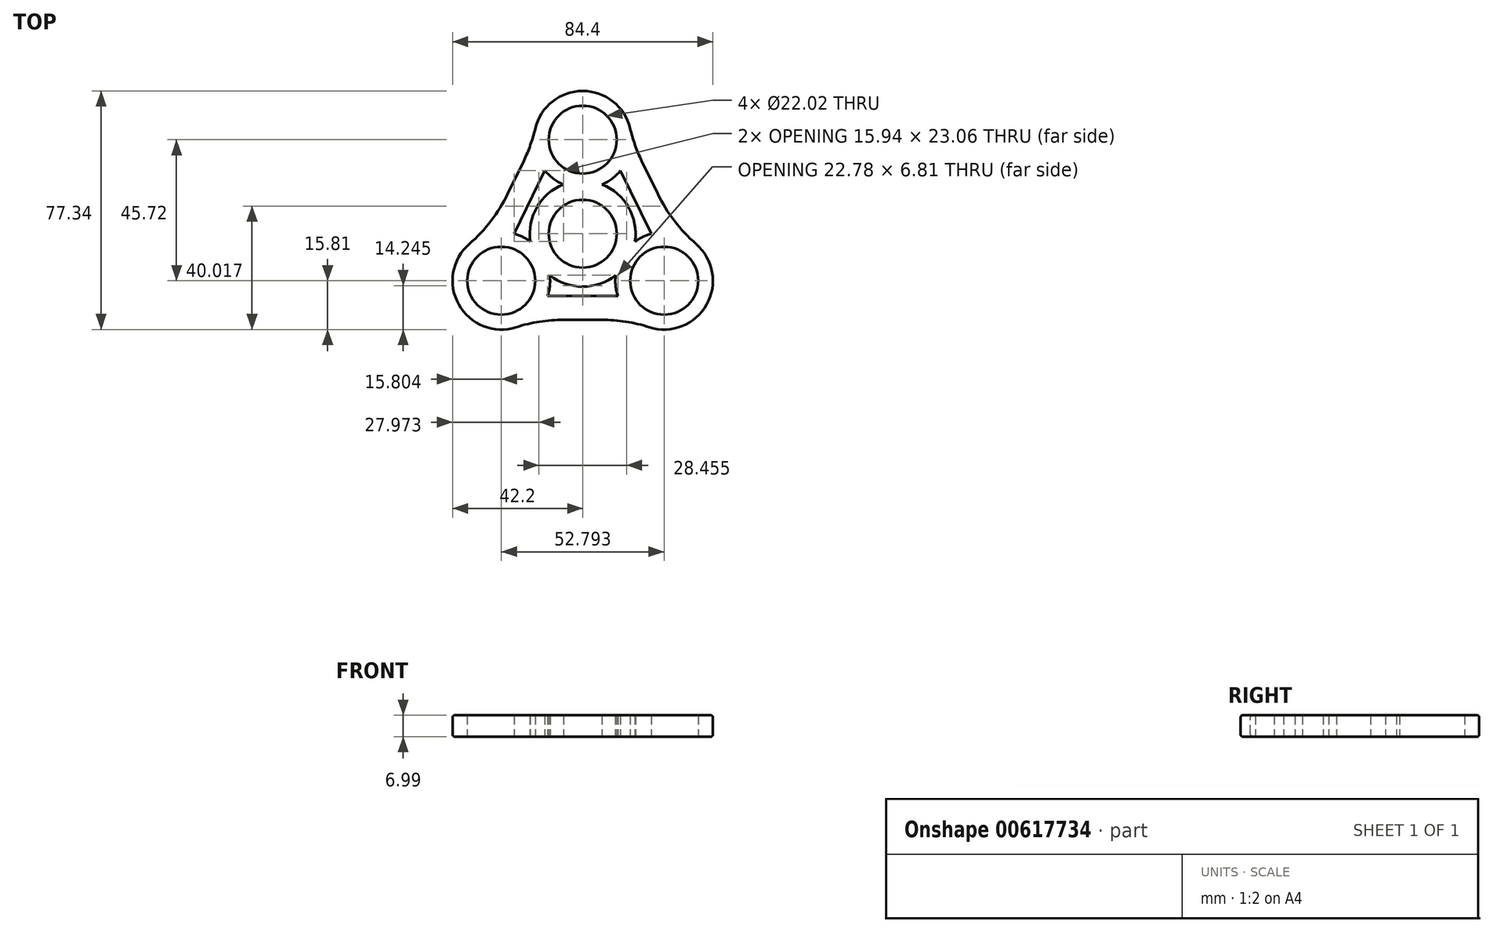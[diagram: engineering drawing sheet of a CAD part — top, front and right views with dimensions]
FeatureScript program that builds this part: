
annotation { "Feature Type Name" : "Feature", "Feature Type Description" : "" }
export const myFeature = defineFeature(function(context is Context, id is Id, definition is map)
    precondition{}
    {
        {
            var Q0;
            Q0=qCreatedBy(makeId("Top.planeOp"),FACE);
            var sketch = newSketch(context, id + "F0", { "sketchPlane" : qUnion([Q0])});
            skCircle(sketch, "E0", {"center": v(0, 0) * mm, "radius": 11.01 * mm});
            skLineSegment(sketch, "E1", {"start": v(0, 0) * mm, "end": v(0, 30.48) * mm});
            skLineSegment(sketch, "E2", {"start": v(0, 0) * mm, "end": v(26.4, -15.24) * mm});
            skLineSegment(sketch, "E3", {"start": v(0, 0) * mm, "end": v(-26.4, -15.24) * mm});
            skCircle(sketch, "E4", {"center": v(0, 30.48) * mm, "radius": 11.01 * mm});
            skCircle(sketch, "E5", {"center": v(26.4, -15.24) * mm, "radius": 11.01 * mm});
            skCircle(sketch, "E6", {"center": v(-26.4, -15.24) * mm, "radius": 11.01 * mm});
            skCircle(sketch, "E7", {"center": v(0, 30.48) * mm, "radius": 15.8 * mm});
            skCircle(sketch, "E8", {"center": v(26.4, -15.24) * mm, "radius": 15.8 * mm});
            skCircle(sketch, "E9", {"center": v(-26.4, -15.24) * mm, "radius": 15.8 * mm});
            skCircle(sketch, "E10", {"center": v(0, 0) * mm, "radius": 17.15 * mm});
            skLineSegment(sketch, "E11", {"start": v(15.8, 30.48) * mm, "end": v(30.6, 0) * mm});
            skLineSegment(sketch, "E12", {"start": v(-15.8, 30.48) * mm, "end": v(-30.6, 0) * mm});
            skLineSegment(sketch, "E13", {"start": v(-16.94, -27.9) * mm, "end": v(16.94, -27.9) * mm});
            skLineSegment(sketch, "E14", {"start": v(-12.26, 20.5) * mm, "end": v(-22.2, 0) * mm});
            skLineSegment(sketch, "E15", {"start": v(12.26, 20.5) * mm, "end": v(22.2, 0) * mm});
            skLineSegment(sketch, "E16", {"start": v(-11.4, -20.21) * mm, "end": v(11.4, -20.21) * mm});
            skSolve(sketch);
        }
        {
            var Q0;
            Q0 = qSketchRegion(id + "F0", true);
            var Q1;
            {var subQ1=sQuery(id+"F0.wireOp",EDGE,"E1");var subQ5=sQuery(id+"F0.wireOp",EDGE,"E0");var subQ6=makeQuery(id+"F0.imprint","INTERSECT",VERTEX,{"derivedFrom":[subQ5,subQ1]});Q1=makeQuery(id+"F0.imprint","IMPRINT",FACE,{"disambiguationData":[TD([[makeQuery(id+"F0.imprint","IMPRINT",EDGE,{"disambiguationData":[TD([[subQ6,1.0]])],"derivedFrom":subQ5}),-1.0]])]});}
            var Q2;
            {var subQ5=sQuery(id+"F0.wireOp",EDGE,"E3");var subQ6=sQuery(id+"F0.wireOp",EDGE,"E0");var subQ7=makeQuery(id+"F0.imprint","INTERSECT",VERTEX,{"derivedFrom":[subQ6,subQ5]});Q2=makeQuery(id+"F0.imprint","IMPRINT",FACE,{"disambiguationData":[TD([[makeQuery(id+"F0.imprint","IMPRINT",EDGE,{"disambiguationData":[TD([[subQ7,-1.0]])],"derivedFrom":subQ6}),-1.0]])]});}
            var Q3;
            {var subQ5=sQuery(id+"F0.wireOp",EDGE,"E0");var subQ7=sQuery(id+"F0.wireOp",EDGE,"E3");var subQ8=makeQuery(id+"F0.imprint","INTERSECT",VERTEX,{"derivedFrom":[subQ5,subQ7]});Q3=makeQuery(id+"F0.imprint","IMPRINT",FACE,{"disambiguationData":[TD([[makeQuery(id+"F0.imprint","IMPRINT",EDGE,{"disambiguationData":[TD([[subQ8,1.0]])],"derivedFrom":subQ5}),-1.0]])]});}
            var Q4;
            {var subQ0=sQuery(id+"F0.wireOp",EDGE,"E10");var subQ1=sQuery(id+"F0.wireOp",EDGE,"E2");var subQ2=makeQuery(id+"F0.imprint","INTERSECT",VERTEX,{"derivedFrom":[subQ1,subQ0]});Q4=makeQuery(id+"F0.imprint","IMPRINT",FACE,{"disambiguationData":[TD([[makeQuery(id+"F0.imprint","IMPRINT",EDGE,{"disambiguationData":[TD([[subQ2,1.0]])],"derivedFrom":subQ1}),-1.0]])]});}
            var Q5;
            {var subQ0=sQuery(id+"F0.wireOp",EDGE,"E10");var subQ1=sQuery(id+"F0.wireOp",EDGE,"E2");var subQ2=makeQuery(id+"F0.imprint","INTERSECT",VERTEX,{"derivedFrom":[subQ1,subQ0]});Q5=makeQuery(id+"F0.imprint","IMPRINT",FACE,{"disambiguationData":[TD([[makeQuery(id+"F0.imprint","IMPRINT",EDGE,{"disambiguationData":[TD([[subQ2,1.0]])],"derivedFrom":subQ1}),1.0]])]});}
            var Q6;
            {var subQ0=sQuery(id+"F0.wireOp",EDGE,"E10");var subQ1=sQuery(id+"F0.wireOp",EDGE,"E1");var subQ2=makeQuery(id+"F0.imprint","INTERSECT",VERTEX,{"derivedFrom":[subQ1,subQ0]});Q6=makeQuery(id+"F0.imprint","IMPRINT",FACE,{"disambiguationData":[TD([[makeQuery(id+"F0.imprint","IMPRINT",EDGE,{"disambiguationData":[TD([[subQ2,1.0]])],"derivedFrom":subQ1}),-1.0]])]});}
            var Q7;
            {var subQ0=sQuery(id+"F0.wireOp",EDGE,"E10");var subQ1=sQuery(id+"F0.wireOp",EDGE,"E1");var subQ2=makeQuery(id+"F0.imprint","INTERSECT",VERTEX,{"derivedFrom":[subQ1,subQ0]});Q7=makeQuery(id+"F0.imprint","IMPRINT",FACE,{"disambiguationData":[TD([[makeQuery(id+"F0.imprint","IMPRINT",EDGE,{"disambiguationData":[TD([[subQ2,1.0]])],"derivedFrom":subQ1}),1.0]])]});}
            var Q8;
            {var subQ0=sQuery(id+"F0.wireOp",EDGE,"E10");var subQ1=sQuery(id+"F0.wireOp",EDGE,"E3");var subQ2=makeQuery(id+"F0.imprint","INTERSECT",VERTEX,{"derivedFrom":[subQ1,subQ0]});Q8=makeQuery(id+"F0.imprint","IMPRINT",FACE,{"disambiguationData":[TD([[makeQuery(id+"F0.imprint","IMPRINT",EDGE,{"disambiguationData":[TD([[subQ2,1.0]])],"derivedFrom":subQ1}),-1.0]])]});}
            var Q9;
            {var subQ0=sQuery(id+"F0.wireOp",EDGE,"E10");var subQ1=sQuery(id+"F0.wireOp",EDGE,"E3");var subQ2=makeQuery(id+"F0.imprint","INTERSECT",VERTEX,{"derivedFrom":[subQ1,subQ0]});Q9=makeQuery(id+"F0.imprint","IMPRINT",FACE,{"disambiguationData":[TD([[makeQuery(id+"F0.imprint","IMPRINT",EDGE,{"disambiguationData":[TD([[subQ2,1.0]])],"derivedFrom":subQ1}),1.0]])]});}
            extrude(context, id + "F1", {"entities" : qUnion([Q0, Q1, Q2, Q3, Q4, Q5, Q6, Q7, Q8, Q9]), "depth" : 7 * mm, "offsetDistance" : 25.4 * mm});
        }
        {
            var Q0;
            Q0=makeQuery(id+"F1.opExtrude","SWEPT_EDGE",EDGE,{"disambiguationData":[OSD([sQuery(id+"F0.wireOp",EDGE,"E8"),sQuery(id+"F0.wireOp",EDGE,"E13")])]});
            var Q1;
            Q1=makeQuery(id+"F1.opExtrude","SWEPT_EDGE",EDGE,{"disambiguationData":[OSD([sQuery(id+"F0.wireOp",EDGE,"E9"),sQuery(id+"F0.wireOp",EDGE,"E13")])]});
            var Q2;
            Q2=makeQuery(id+"F1.opExtrude","SWEPT_EDGE",EDGE,{"disambiguationData":[OSD([sQuery(id+"F0.wireOp",EDGE,"E7"),sQuery(id+"F0.wireOp",EDGE,"E11")])]});
            var Q3;
            Q3=makeQuery(id+"F1.opExtrude","SWEPT_EDGE",EDGE,{"disambiguationData":[OSD([sQuery(id+"F0.wireOp",EDGE,"E8"),sQuery(id+"F0.wireOp",EDGE,"E11")])]});
            var Q4;
            Q4=makeQuery(id+"F1.opExtrude","SWEPT_EDGE",EDGE,{"disambiguationData":[OSD([sQuery(id+"F0.wireOp",EDGE,"E7"),sQuery(id+"F0.wireOp",EDGE,"E12")])]});
            var Q5;
            Q5=makeQuery(id+"F1.opExtrude","SWEPT_EDGE",EDGE,{"disambiguationData":[OSD([sQuery(id+"F0.wireOp",EDGE,"E9"),sQuery(id+"F0.wireOp",EDGE,"E12")])]});
            fillet(context, id + "F2", {"entities" : qUnion([Q0, Q1, Q2, Q3, Q4, Q5]), "radius" : 50.8 * mm, "tangentPropagation" : true, "allowEdgeOverflow" : false});
        }
        {
            var Q0;
            Q0=makeQuery(id+"F1.opExtrude","CAP_EDGE",EDGE,{"disambiguationData":[OSD([sQuery(id+"F0.wireOp",EDGE,"E13")])],"isStart":true});
            fillet(context, id + "F3", {"entities" : qUnion([Q0]), "radius" : 0.76 * mm, "tangentPropagation" : true, "allowEdgeOverflow" : false});
        }
        {
            var Q0;
            Q0=makeQuery(id+"F1.opExtrude","CAP_EDGE",EDGE,{"disambiguationData":[OSD([sQuery(id+"F0.wireOp",EDGE,"E12")])],"isStart":false});
            fillet(context, id + "F4", {"entities" : qUnion([Q0]), "radius" : 0.76 * mm, "tangentPropagation" : true, "allowEdgeOverflow" : false});
        }
    });
